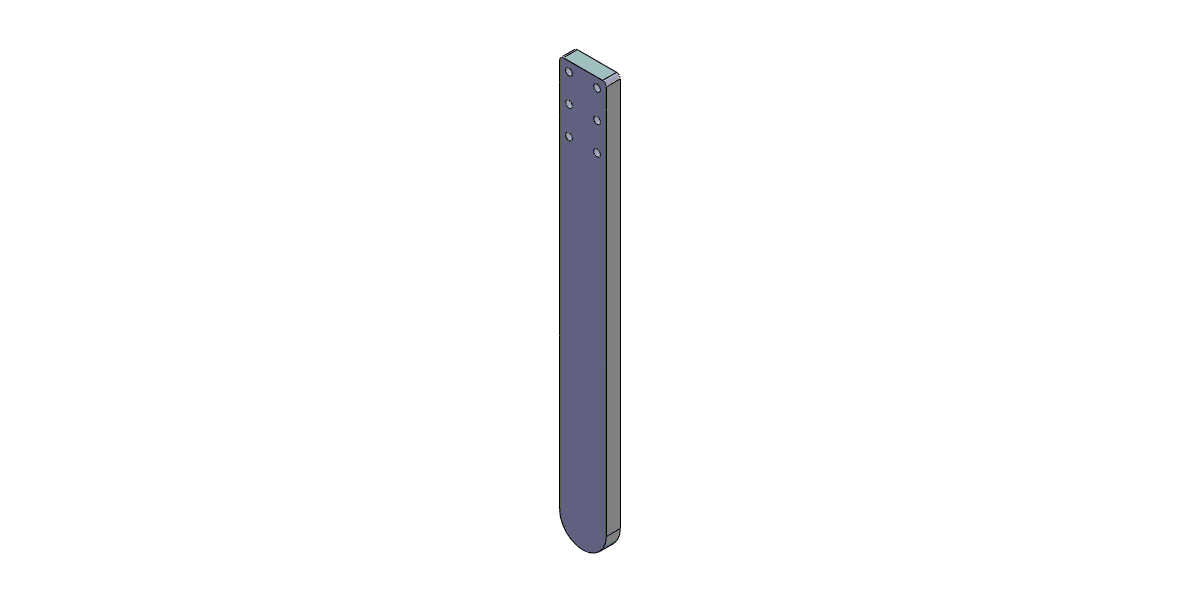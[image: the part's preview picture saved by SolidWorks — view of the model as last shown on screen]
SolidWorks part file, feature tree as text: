
SOLIDWORKS PART (.sldprt)
format: sldprt  version: not decoded by parser v0  size: 151,552 bytes
history: native  units: mm
features: sketch x4, material x1, extrude x1, cut_extrude x1, fillet x1, hole x1 (+13 scaffold rows collapsed)
feature tree (22):
  scaffold x13  (default folders/planes/origin — collapsed)
  material  "7079 Alloy"
  sketch  "Sketch1"  dims[D1=31.75mm D2=31.75mm D3=292.1mm D4=~149.975094mm]
  extrude  "Boss-Extrude1"  Depth=9.525mm
  sketch  "Sketch2"  dims[c1.D1=~69.821207mm c1.D2=~31.748727mm c2.D1=31.75mm c2.D2=50.8mm c2.D3=50.8mm]
  cut_extrude  "Cut-Extrude1"  [1 undecoded]
  fillet  "Fillet1"  Radius=2.54mm
  hole  "#8 Clearance Hole1"  Diameter=4.4958mm Depth=7.62mm
  sketch  "Sketch3"
  sketch  "Sketch4"  dims[Thru Hole Dia.=4.4958mm Thru Hole Depth=7.62mm]
decode coverage: 6 of 8 modeling features carry decoded parameters
note: ~ marks probable driven/reference dimensions
note: 1 parameter value undecoded
note: suppression state not decoded; provenance and decode notes live in map.json
